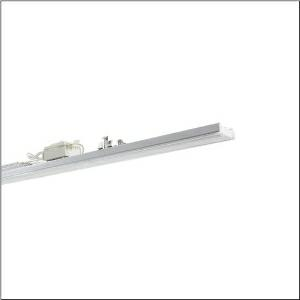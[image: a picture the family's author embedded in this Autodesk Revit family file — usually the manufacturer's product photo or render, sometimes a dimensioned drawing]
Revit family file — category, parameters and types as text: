
# Revit family: licross_r__21_recessed_mo_52tl10de45xg_9f5a
name_source: partatom
category: Lighting Fixtures
units: mm (PartAtom-declared; Revit-internal decimal feet)

## family parameters
Cut with Voids When Loaded = No
Host = Face
Light Source = No
Part Type = Normal
Room Calculation Point = No
Round Connector Dimension = Use Diameter
Shared = No

## types (1)
- --- (1 x LED, 5000 lm, 29.9 W, 4000K)
    Apparent Load = 30 VA
    CIE Flux Codes = 50 81 96 100 100
    Color Rendering = 80
    Color Temperature = 4000K
    Default Elevation = 1800 mm
    Description = Licross® 21 Recessed MO, luminaire insert, of sheet steel, galvanised, coil coated, white, length: 750mm, width: 66mm, height: 67mm, LED rated luminous flux: 5.000lm, light colour: 840, control gear: DALI 2, with plug, 5-pole, with phase selection, mains connection: 220..240V, AC, 50/60Hz, rated input power: 30W, halogen-free wiring, primary optical cover: cover, of PMMA, light emission: direct distribution, primary light characteristic: symmetric, protection rating (complete): IP40, insulation class (complete): insulation class I (protective earthing), certification: CE, ENEC, VDE, UKCA, protection symbol: D if used in an environment without relevant dust loads with corresponding accessories, impact resistance: IK06, permissible ambient temperature for indoor applications: -25..+35°C, corresponds to IFS (International Featured Standards) requirements for safety and quality in the food industry, reducing of maximum allowable ambient temperature of 5°C with ceiling mounting, LABS conformity tested according to VDMA 24364:2018-05, packaging unit: 1 piece
    Height = 58 mm
    Lamp = 1 x LED
    Lamp Light Flux = 5000 lm
    Lamp Power = 29.9 W
    Lamp count = 1
    Length = 750 mm
    Luminous efficacy = 167 lm/W
    Manufacturer = Siteco
    ModVariant = No
    Model = 52TL10DE45XG
    Mounting Place = Ceiling
    Mounting Type = Pendant
    Number of Poles = 1
    OnlyDefault = Yes
    Power Factor = 1
    Product Name = Licross® 21 Recessed MO
    Product group = luminaire insert
    ProductGroupID = 902
    Protection Class = Protection class I
    Protection Degree = IP 40
    RLX_Detail_Level = 1
    RLX_Emergency_Light_Flux = 0 lm
    RLX_Emergency_Type = 0
    RLX_Emergency_Type_DB = No
    RlxData = <blob elided: 28469 chars, md5=18cf9d66>
    Socket = socket
    Standby Power = 0 W
    System Light Flux = 5000 lm
    System Power = 30 W
    Type Comments = factory setting: luminous flux: 100 % | dim-lin: 254 | 390 mA
    Type Image = l_1296930.jpg
    URL = http://relux.com
    VarID = @adj_127676
    Voltage = 0 V
    Weight = 0.00 kg
    Width = 66 mm

## geometry (parser evidence)
native form markers: Blend x4, Sweep x9
no freeform markers — native parametric forms only
